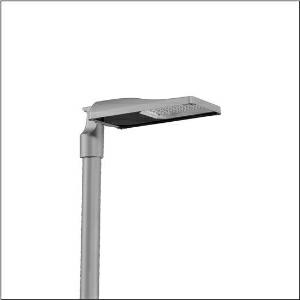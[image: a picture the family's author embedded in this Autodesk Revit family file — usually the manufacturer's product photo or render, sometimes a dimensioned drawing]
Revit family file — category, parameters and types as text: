
# Revit family: streetlight_sl_31_mini___st1_0a_5xh6d31b08ga_f949
name_source: partatom
category: Lighting Fixtures
units: mm (PartAtom-declared; Revit-internal decimal feet)

## family parameters
Cut with Voids When Loaded = No
Host = Face
Light Source = No
Part Type = Normal
Room Calculation Point = No
Round Connector Dimension = Use Diameter
Shared = No

## types (1)
- --- (1 x LED, 5710 lm, 37.3 W, 3000K)
    Apparent Load = 37 VA
    CIE Flux Codes = 37 72 97 100 100
    Color Rendering = 70
    Color Temperature = 3000K
    Default Elevation = 1800 mm
    Description = Streetlight SL 31 mini Easy, LST, Desk-Remote mast luminaire for post-top, side-entry; light control with lens of PMMA; light distribution: ST1.0a, direct asymmetric distribution, for standard-compliant lighting for roads and squares; LED: luminous flux: 5.710lm, light colour: 730, colour temperature: 3000K; luminous efficacy: 153,1lm/W; control: pre-setting: linear dimming characteristic, flexible luminous flux parameterisation, time-dependent luminous flux control, constant luminous flux control, power reduction, intelligent temperature release in ECG and LED module, overheat protection; luminaire housing, of diecast aluminium, Siteco® metallic grey (DB 702S), corrosivity category C5 high according to DIN EN ISO 12944; cover of toughened safety glass, transparent, opened without tools; mast flange of diecast aluminium, Siteco® metallic grey (DB 702S), spigot size: 76/60mm, mast flange included unmounted; with cable H07RN-F 3x 1.5mm², cable length: 6,5m, connection cable pre-assembled; mains connection: 220..240V, AC, 50/60Hz; power consumption (at start of service life): 37,3W / (at end of service life): 38,7W / (with reduced operation 50%): 17,5W; protection rating (complete): IP66; insulation class (complete): insulation class II (safety insulation); impact resistance: IK09; certification: CE, ENEC, ENEC+, VDE, UKCA; permissible operating ambient temperature for outdoor applications: -40..+50°C; packaging unit: 1 piece

Light Distribution: ST1.0a
    Height = 76 mm
    Lamp = 1 x LED
    Lamp Light Flux = 5710 lm
    Lamp Power = 37.3 W
    Lamp count = 1
    Length = 547 mm
    Luminous efficacy = 153 lm/W
    Manufacturer = Siteco
    ModVariant = No
    Model = 5XH6D31B08GA
    Number of Poles = 1
    OnlyDefault = Yes
    Power Factor = 1
    Product Name = Streetlight SL 31 mini | ST1.0a
    Product group = mast luminaire | pylon top
    ProductGroupID = 6100
    Protection Class = Protection class II
    Protection Degree = IP 66
    RLX_Detail_Level = 1
    RLX_Emergency_Light_Flux = 0 lm
    RLX_Emergency_Type = 0
    RLX_Emergency_Type_DB = No
    RlxData = <blob elided: 39565 chars, md5=a142d651>
    Socket = socket
    Standby Power = 0 W
    System Light Flux = 5710 lm
    System Power = 37 W
    Type Comments = factory setting: luminous flux: 100 % | dim-lin: 254 | 386 mA
    Type Image = l_1300326.jpg
    URL = http://relux.com
    VarID = @adj_051160
    Voltage = 0 V
    Weight = 0.00 kg
    Width = 265 mm

## geometry (parser evidence)
native form markers: Blend x4, Sweep x10
no freeform markers — native parametric forms only
